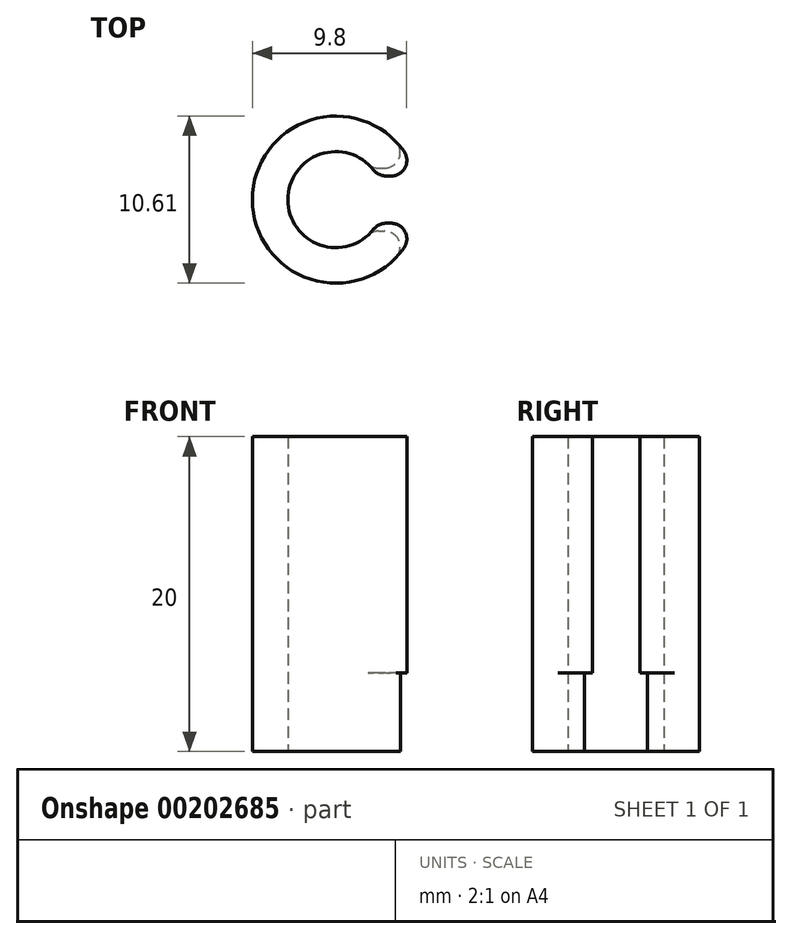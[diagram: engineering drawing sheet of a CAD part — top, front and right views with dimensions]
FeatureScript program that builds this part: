
annotation { "Feature Type Name" : "Feature", "Feature Type Description" : "" }
export const myFeature = defineFeature(function(context is Context, id is Id, definition is map)
    precondition{}
    {
        {
            var Q0;
            Q0=qCreatedBy(makeId("Top.planeOp"),FACE);
            var sketch = newSketch(context, id + "F0", { "sketchPlane" : qUnion([Q0])});
            skArc(sketch, "E0", {"start": v(4.91, 2) * mm, "mid": v(-5.3, 0) * mm, "end": v(4.91, -2) * mm});
            skArc(sketch, "E1", {"start": v(2.3, 2) * mm, "mid": v(-3.05, 0) * mm, "end": v(2.3, -2) * mm});
            skLineSegment(sketch, "E2.trimOffspring", {"start": v(2.3, -2) * mm, "end": v(4.91, -2) * mm});
            skLineSegment(sketch, "E3.trimOffspring", {"start": v(2.3, 2) * mm, "end": v(4.91, 2) * mm});
            skSolve(sketch);
        }
        {
            var Q0;
            Q0=makeQuery(id+"F0.imprint","IMPRINT",FACE,{"disambiguationData":[TD([[makeQuery(id+"F0.imprint","IMPRINT",EDGE,{"derivedFrom":sQuery(id+"F0.wireOp",EDGE,"E0")}),1.0]])]});
            extrude(context, id + "F1", {"entities" : qUnion([Q0]), "depth" : 5 * mm});
        }
        {
            var Q0;
            Q0=makeQuery(id+"F1.opExtrude","SWEPT_EDGE",EDGE,{"disambiguationData":[OSD([sQuery(id+"F0.wireOp",EDGE,"E0"),sQuery(id+"F0.wireOp",EDGE,"E3.trimOffspring")])]});
            var Q1;
            Q1=makeQuery(id+"F1.opExtrude","SWEPT_EDGE",EDGE,{"disambiguationData":[OSD([sQuery(id+"F0.wireOp",EDGE,"E1"),sQuery(id+"F0.wireOp",EDGE,"E3.trimOffspring")])]});
            var Q2;
            Q2=makeQuery(id+"F1.opExtrude","SWEPT_EDGE",EDGE,{"disambiguationData":[OSD([sQuery(id+"F0.wireOp",EDGE,"E1"),sQuery(id+"F0.wireOp",EDGE,"E2.trimOffspring")])]});
            var Q3;
            Q3=makeQuery(id+"F1.opExtrude","SWEPT_EDGE",EDGE,{"disambiguationData":[OSD([sQuery(id+"F0.wireOp",EDGE,"E0"),sQuery(id+"F0.wireOp",EDGE,"E2.trimOffspring")])]});
            fillet(context, id + "F2", {"entities" : qUnion([Q0, Q1, Q2, Q3]), "radius" : 1 * mm, "allowEdgeOverflow" : false});
        }
        {
            var Q0;
            Q0=qCreatedBy(makeId("Top.planeOp"),FACE);
            var sketch = newSketch(context, id + "F3", { "sketchPlane" : qUnion([Q0])});
            skArc(sketch, "E4", {"start": v(5.09, 1.5) * mm, "mid": v(-5.3, 0) * mm, "end": v(5.09, -1.5) * mm});
            skArc(sketch, "E5", {"start": v(2.66, 1.5) * mm, "mid": v(-3.05, 0) * mm, "end": v(2.66, -1.5) * mm});
            skLineSegment(sketch, "E6.trimOffspring", {"start": v(2.66, -1.5) * mm, "end": v(5.09, -1.5) * mm});
            skLineSegment(sketch, "E7.trimOffspring", {"start": v(2.66, 1.5) * mm, "end": v(5.09, 1.5) * mm});
            skSolve(sketch);
        }
        {
            var Q0;
            Q0 = qSketchRegion(id + "F3", true);
            var Q1;
            Q1=makeQuery(id+"F1.opExtrude","CAP_FACE",FACE,{"disambiguationData":[OSD([sQuery(id+"F0.wireOp",EDGE,"E0"),sQuery(id+"F0.wireOp",EDGE,"E1"),sQuery(id+"F0.wireOp",EDGE,"E2.trimOffspring"),sQuery(id+"F0.wireOp",EDGE,"E3.trimOffspring")])],"isStart":false});
            extrude(context, id + "F4", {"entities" : qUnion([Q0]), "operationType" : NewBodyOperationType.ADD, "depth" : 20 * mm, "hasSecondDirection" : true, "secondDirectionBound" : SecondDirectionBoundingType.UP_TO_SURFACE, "secondDirectionOppositeDirection" : false, "secondDirectionBoundEntityFace" : qUnion([Q1]), "secondDirectionDepth" : mm});
        }
        {
            var Q0;
            Q0=makeQuery(id+"F4.opExtrude","SWEPT_EDGE",EDGE,{"disambiguationData":[OSD([sQuery(id+"F3.wireOp",EDGE,"E4"),sQuery(id+"F3.wireOp",EDGE,"E6.trimOffspring")])]});
            var Q1;
            Q1=makeQuery(id+"F4.opExtrude","SWEPT_EDGE",EDGE,{"disambiguationData":[OSD([sQuery(id+"F3.wireOp",EDGE,"E4"),sQuery(id+"F3.wireOp",EDGE,"E7.trimOffspring")])]});
            var Q2;
            Q2=makeQuery(id+"F4.opExtrude","SWEPT_EDGE",EDGE,{"disambiguationData":[OSD([sQuery(id+"F3.wireOp",EDGE,"E5"),sQuery(id+"F3.wireOp",EDGE,"E6.trimOffspring")])]});
            var Q3;
            Q3=makeQuery(id+"F4.opExtrude","SWEPT_EDGE",EDGE,{"disambiguationData":[OSD([sQuery(id+"F3.wireOp",EDGE,"E5"),sQuery(id+"F3.wireOp",EDGE,"E7.trimOffspring")])]});
            fillet(context, id + "F5", {"entities" : qUnion([Q0, Q1, Q2, Q3]), "radius" : 1 * mm, "tangentPropagation" : true, "allowEdgeOverflow" : false});
        }
    });
